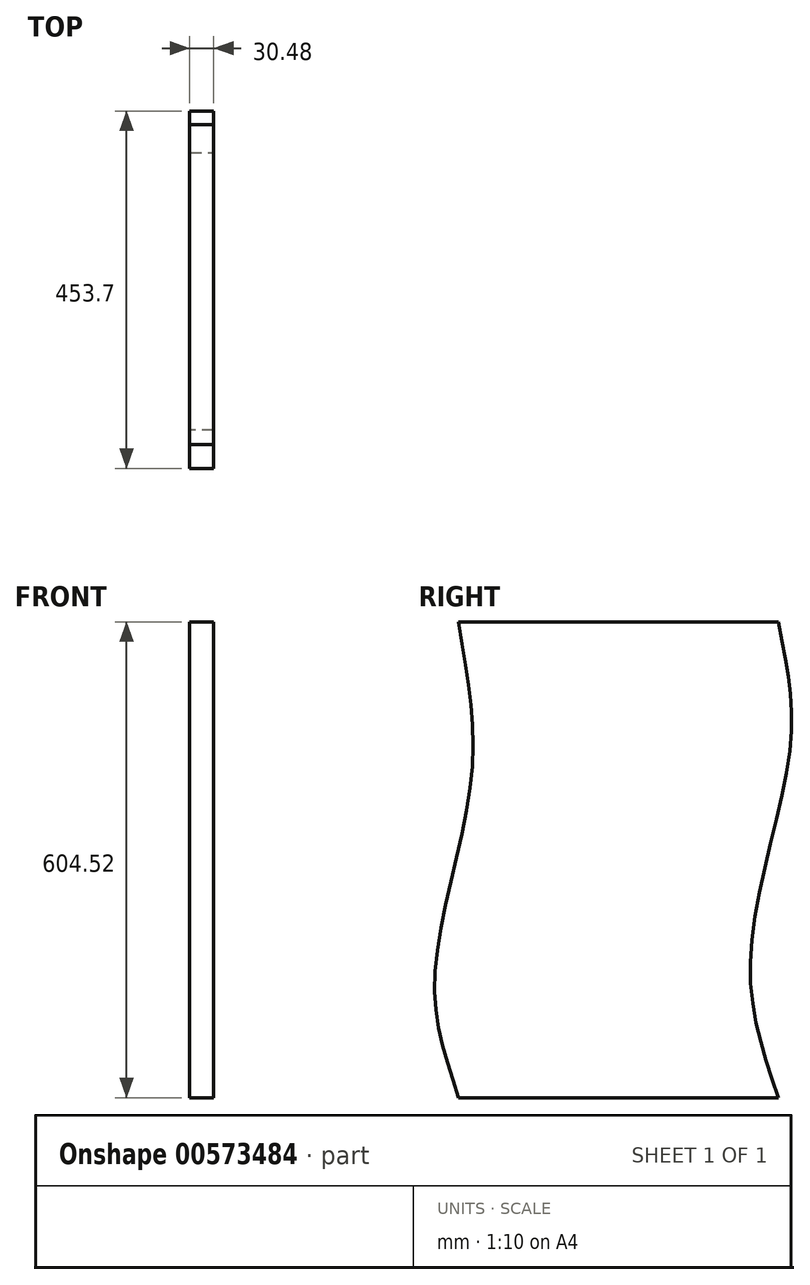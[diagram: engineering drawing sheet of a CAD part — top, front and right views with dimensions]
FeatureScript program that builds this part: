
annotation { "Feature Type Name" : "Feature", "Feature Type Description" : "" }
export const myFeature = defineFeature(function(context is Context, id is Id, definition is map)
    precondition{}
    {
        {
            var Q0;
            Q0=qCreatedBy(makeId("Right.planeOp"),FACE);
            var sketch = newSketch(context, id + "F0", { "sketchPlane" : qUnion([Q0])});
            skLineSegment(sketch, "E0.bottom", {"start": v(0, 0) * mm, "end": v(406.4, 0) * mm});
            skLineSegment(sketch, "E0.top", {"start": v(0, 604.52) * mm, "end": v(406.4, 604.52) * mm});
            skFitSpline(sketch, "E1", {"points": [v(0, 604.52) * mm, v(15.87, 402.68) * mm, v(-30.13, 153.99) * mm, v(0, 0) * mm], "startDerivative": vector(108.28, -657.74) * mm, "endDerivative": vector(168.87, -530.86) * mm});
            skFitSpline(sketch, "E2", {"points": [v(406.4, 604.52) * mm, v(421.25, 444.37) * mm, v(370.94, 181.3) * mm, v(406.4, 0) * mm], "startDerivative": vector(108.74, -570.76) * mm, "endDerivative": vector(187.27, -548.06) * mm});
            skSolve(sketch);
        }
        {
            var Q0;
            Q0=makeQuery(id+"F0.imprint","IMPRINT",FACE,{"disambiguationData":[TD([[makeQuery(id+"F0.imprint","IMPRINT",EDGE,{"derivedFrom":sQuery(id+"F0.wireOp",EDGE,"E0.bottom")}),1.0]])]});
            extrude(context, id + "F1", {"entities" : qUnion([Q0]), "depth" : 30.48 * mm, "offsetDistance" : 25.4 * mm});
        }
    });
